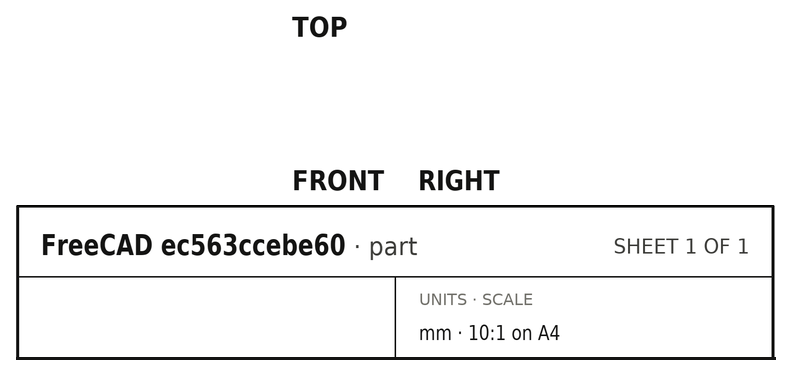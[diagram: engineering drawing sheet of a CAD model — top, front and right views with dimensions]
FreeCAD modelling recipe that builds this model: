
FCSTD DOCUMENT  (FreeCAD 0.21R33668 +26 (Git))
Label: point
License: All rights reserved
LicenseURL: https://en.wikipedia.org/wiki/All_rights_reserved
objects: Sketcher::SketchObject×1, PartDesign::Revolution×1, PartDesign::Body×1
note: 4 computed .brp shape members not serialized (recipe doc carries the construction recipe); baked Part::Feature solids carry a one-line shape summary decoded from their .brp

FEATURE [Sketcher::SketchObject] Sketch
  FullyConstrained = false
  MapMode = 5
  Placement = pos=(0,0,0) rot=(1,0,0;1.5708rad)
  Support = -> [XZ_Plane]
  sketch-geometry (2):
    g0: ArcOfCircle CenterX=0 CenterY=0 CenterZ=0 NormalX=0 NormalY=0 NormalZ=1 AngleXU=0 Radius=0.0005 StartAngle=0 EndAngle=3.14159
    g1: LineSegment StartX=-0.0005 StartY=0 StartZ=0 EndX=0.0005 EndY=0 EndZ=0
  constraints (5):
    c: Coincident(g0,g-1)
    c: Diameter(g0) = 0.001
    c: PointOnObject(g1,g0)
    c: PointOnObject(g1,g0)
    c: Horizontal(g1)
FEATURE [PartDesign::Revolution] Revolution
  Angle = 360
  Axis = (1,0,0)
  Base = (0,0,0)
  Midplane = true
  Placement = pos=(0,0,0) rot=(1,0,0;1.5708rad)
  Profile = -> Sketch
  ReferenceAxis = -> X_Axis
FEATURE [PartDesign::Body] Body
  Group = -> [Sketch,Revolution]
  Origin = -> Origin
  Tip = -> Revolution
